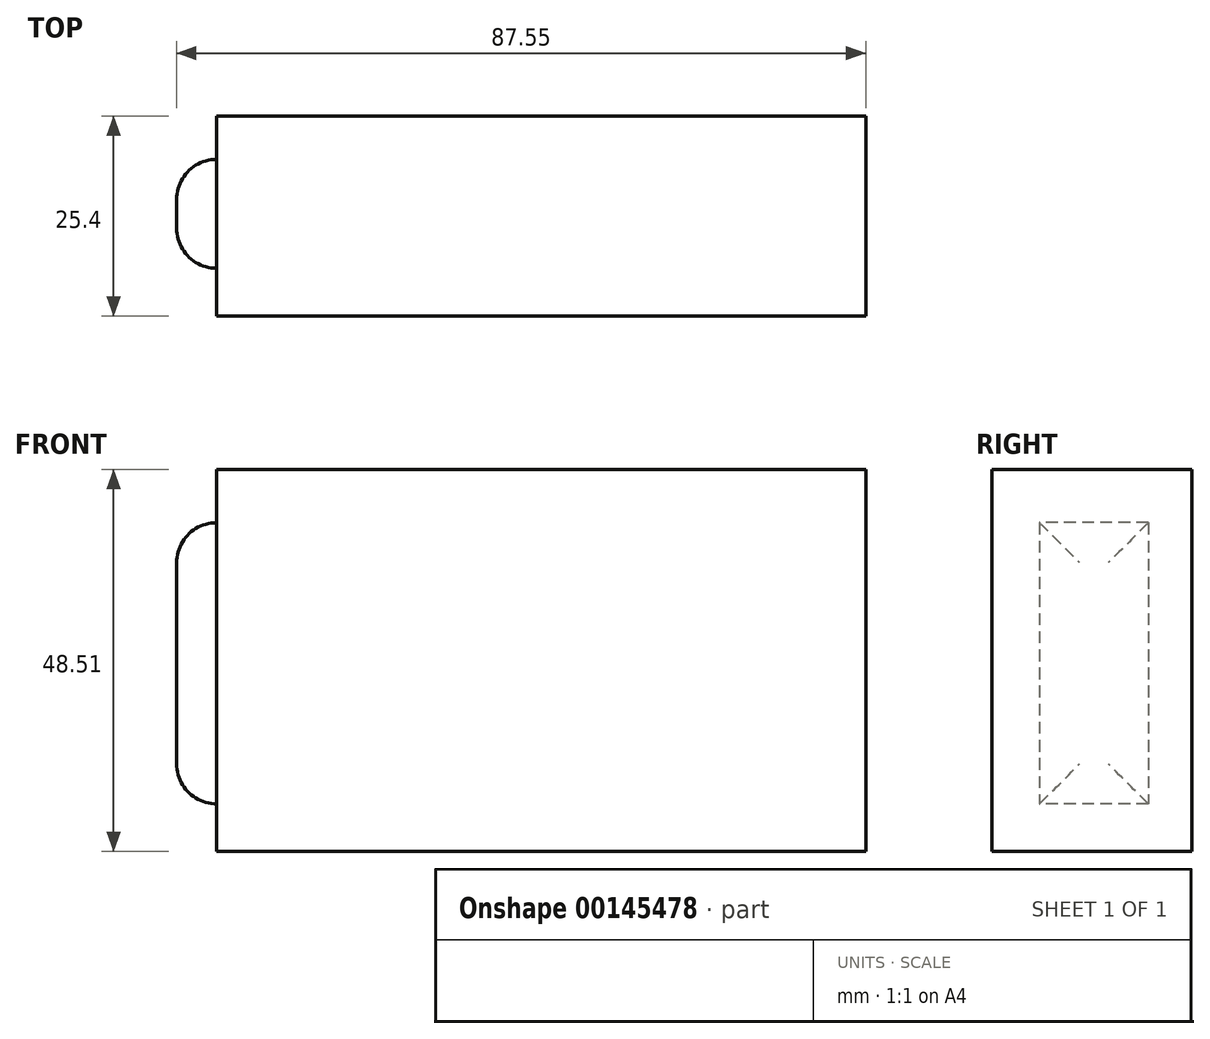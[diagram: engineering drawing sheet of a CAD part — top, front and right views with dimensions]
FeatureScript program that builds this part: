
annotation { "Feature Type Name" : "Feature", "Feature Type Description" : "" }
export const myFeature = defineFeature(function(context is Context, id is Id, definition is map)
    precondition{}
    {
        {
            var Q0;
            Q0=qCreatedBy(makeId("Front.planeOp"),FACE);
            var sketch = newSketch(context, id + "F0", { "sketchPlane" : qUnion([Q0])});
            skLineSegment(sketch, "E0.bottom", {"start": v(-36.87, 20.13) * mm, "end": v(45.6, 20.13) * mm});
            skLineSegment(sketch, "E0.top", {"start": v(-36.87, -28.38) * mm, "end": v(45.6, -28.38) * mm});
            skLineSegment(sketch, "E0.left", {"start": v(-36.87, 20.13) * mm, "end": v(-36.87, -28.38) * mm});
            skLineSegment(sketch, "E0.right", {"start": v(45.6, 20.13) * mm, "end": v(45.6, -28.38) * mm});
            skSolve(sketch);
        }
        {
            var Q0;
            Q0=makeQuery(id+"F0.imprint","IMPRINT",FACE,{"disambiguationData":[TD([[makeQuery(id+"F0.imprint","IMPRINT",EDGE,{"derivedFrom":sQuery(id+"F0.wireOp",EDGE,"E0.bottom")}),-1.0]])]});
            extrude(context, id + "F1", {"entities" : qUnion([Q0]), "depth" : 25.4 * mm});
        }
        {
            var Q0;
            Q0=makeQuery(id+"F1.opExtrude","SWEPT_FACE",FACE,{"disambiguationData":[OSD([sQuery(id+"F0.wireOp",EDGE,"E0.left")])]});
            var sketch = newSketch(context, id + "F2", { "sketchPlane" : qUnion([Q0])});
            skLineSegment(sketch, "E1.bottom", {"start": v(5.5, 13.38) * mm, "end": v(19.32, 13.38) * mm});
            skLineSegment(sketch, "E1.top", {"start": v(5.5, -22.35) * mm, "end": v(19.32, -22.35) * mm});
            skLineSegment(sketch, "E1.left", {"start": v(5.5, 13.38) * mm, "end": v(5.5, -22.35) * mm});
            skLineSegment(sketch, "E1.right", {"start": v(19.32, 13.38) * mm, "end": v(19.32, -22.35) * mm});
            skSolve(sketch);
        }
        {
            var Q0;
            Q0=makeQuery(id+"F2.imprint","IMPRINT",FACE,{"disambiguationData":[TD([[makeQuery(id+"F2.imprint","IMPRINT",EDGE,{"derivedFrom":sQuery(id+"F2.wireOp",EDGE,"E1.bottom")}),-1.0]])]});
            extrude(context, id + "F3", {"entities" : qUnion([Q0]), "operationType" : NewBodyOperationType.ADD, "depth" : 5.08 * mm});
        }
        {
            var Q0;
            Q0=makeQuery(id+"F3.opExtrude","CAP_EDGE",EDGE,{"disambiguationData":[OSD([sQuery(id+"F2.wireOp",EDGE,"E1.top")])],"isStart":false});
            var Q1;
            Q1=makeQuery(id+"F3.opExtrude","CAP_EDGE",EDGE,{"disambiguationData":[OSD([sQuery(id+"F2.wireOp",EDGE,"E1.left")])],"isStart":false});
            var Q2;
            Q2=makeQuery(id+"F3.opExtrude","CAP_EDGE",EDGE,{"disambiguationData":[OSD([sQuery(id+"F2.wireOp",EDGE,"E1.right")])],"isStart":false});
            var Q3;
            Q3=makeQuery(id+"F3.opExtrude","CAP_EDGE",EDGE,{"disambiguationData":[OSD([sQuery(id+"F2.wireOp",EDGE,"E1.bottom")])],"isStart":false});
            fillet(context, id + "F4", {"entities" : qUnion([Q0, Q1, Q2, Q3]), "radius" : 5.08 * mm, "tangentPropagation" : true, "allowEdgeOverflow" : false});
        }
    });
